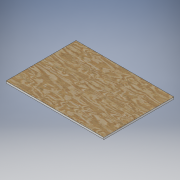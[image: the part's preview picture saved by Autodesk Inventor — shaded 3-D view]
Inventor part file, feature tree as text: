
AUTODESK INVENTOR PART (.ipt)
format: ipt  version: 2018.2 (Build 222227000, 227)  size: 111,616 bytes
history: native  units: in
note: dims shown in document units (in); Inventor stores cm internally (conversion verified against a paired STEP export)
features: extrude x1, sketch x1
ambient origin geometry x8: Origin, YZ Plane, XZ Plane, XY Plane, X Axis, Y Axis, Z Axis, Center Point
bodies: Solid1 (feature_tree)
feature tree (2):
  extrude  "Extrusion1"  Depth=0.75in
  sketch  "Sketch1"  dims[d0=39.398in d1=0.75in d2=28.228in d3=0.0in]
